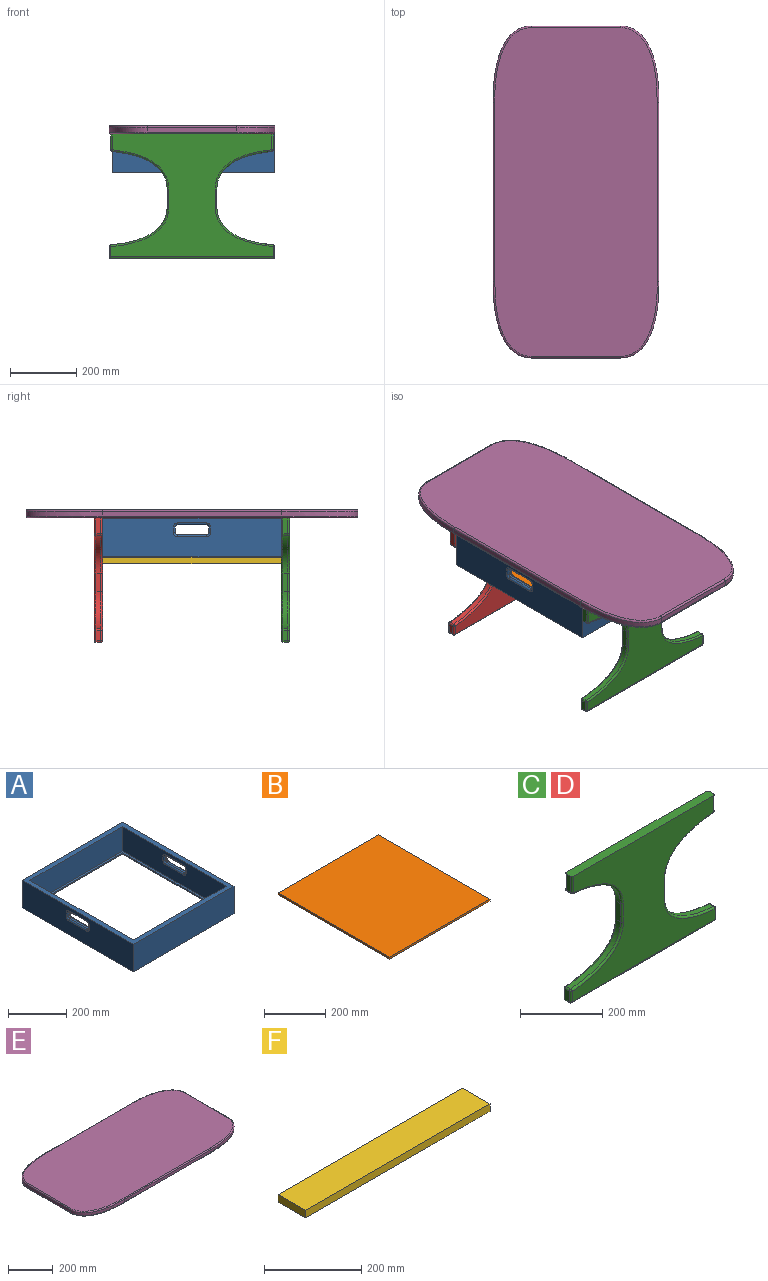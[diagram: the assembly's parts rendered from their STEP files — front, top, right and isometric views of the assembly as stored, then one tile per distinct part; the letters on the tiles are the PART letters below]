
ASSEMBLY  parts=6 mates=5
PART A: 68 faces, bbox 488x538x115 mm
  f0: plane 500x101.8mm, normal (1,0,0), area 46319.6mm2, adj f2,f3,f12,f27,f32,f33,f36,f37
  f1: plane 500x101.8mm, normal (-1,0,0), area 46319.6mm2, adj f2,f3,f12,f50,f51,f54,f55,f58
  f2: plane 450x101.8mm, normal (0,-1,0), area 45810mm2, adj f0,f1,f12,f62
  f3: plane 450x101.8mm, normal (0,1,0), area 45810mm2, adj f0,f1,f12,f62
  f4: plane 538x115mm, normal (-1,0,0), area 57289.6mm2, adj f8,f9,f12,f13,f22,f23,f24,f25
  f5: plane 500x5mm, normal (1,0,0), area 2500mm2, adj f10,f11,f13,f63
  f6: plane 500x5mm, normal (-1,0,0), area 2500mm2, adj f10,f11,f13,f63
  f7: plane 538x115mm, normal (1,0,0), area 57289.6mm2, adj f8,f9,f12,f13,f42,f43,f44,f46
  f8: plane 488x115mm, normal (0,1,0), area 56120mm2, adj f4,f7,f12,f13
  f9: plane 488x115mm, normal (0,-1,0), area 56120mm2, adj f4,f7,f12,f13
  f10: plane 450x5mm, normal (0,-1,0), area 2250mm2, adj f5,f6,f13,f63
  f11: plane 450x5mm, normal (0,1,0), area 2250mm2, adj f5,f6,f13,f63
  f12: plane 538x488mm, normal (0,0,1), area 37544mm2, adj f0,f1,f2,f3,f4,f7,f8,f9
  f13: plane 538x488mm, normal (0,0,-1), area 37544mm2, adj f4,f5,f6,f7,f8,f9,f10,f11
  f14: plane 18x7mm, normal (0,1,0), area 126mm2, adj f45,f46,f55,f56
  f15: plane 88x7mm, normal (0,0,1), area 616mm2, adj f42,f45,f49,f50
  f16: plane 18x7mm, normal (0,-1,0), area 126mm2, adj f48,f49,f57,f58
  f17: plane 88x7mm, normal (0,0,-1), area 616mm2, adj f47,f56,f57,f61
  f18: plane 88x7mm, normal (0,0,-1), area 616mm2, adj f30,f35,f38,f41
  f19: plane 18x7mm, normal (0,-1,0), area 126mm2, adj f28,f29,f37,f38
  f20: plane 88x7mm, normal (0,0,1), area 616mm2, adj f22,f26,f27,f28
  f21: plane 18x7mm, normal (0,1,0), area 126mm2, adj f25,f26,f35,f36
  f22: cylinder r=6mm len=88mm, axis (0,-1,0), area 829.4mm2, adj f4,f20,f23,f24
  f23: torus R=12mm, axis (1,0,0), area 121.1mm2, adj f4,f22,f25,f26
  f24: torus R=12mm, axis (1,0,0), area 121.1mm2, adj f4,f22,f28,f29
  f25: cylinder r=6mm len=18mm, axis (0,0,1), area 169.6mm2, adj f4,f21,f23,f31
  f26: cylinder r=6mm len=7mm, axis (-1,0,0), area 66mm2, adj f20,f21,f23,f32
  f27: cylinder r=6mm len=88mm, axis (0,-1,0), area 829.4mm2, adj f0,f20,f32,f33
  f28: cylinder r=6mm len=7mm, axis (1,0,0), area 66mm2, adj f19,f20,f24,f33
  f29: cylinder r=6mm len=18mm, axis (0,0,-1), area 169.6mm2, adj f4,f19,f24,f34
  f30: cylinder r=6mm len=88mm, axis (0,1,0), area 829.4mm2, adj f4,f18,f31,f34
  f31: torus R=12mm, axis (1,0,0), area 121.1mm2, adj f4,f25,f30,f35
  f32: torus R=12mm, axis (1,0,0), area 121.1mm2, adj f0,f26,f27,f36
  f33: torus R=12mm, axis (1,0,0), area 121.1mm2, adj f0,f27,f28,f37
  f34: torus R=12mm, axis (1,0,0), area 121.1mm2, adj f4,f29,f30,f38
  f35: cylinder r=6mm len=7mm, axis (1,0,0), area 66mm2, adj f18,f21,f31,f39
  f36: cylinder r=6mm len=18mm, axis (0,0,1), area 169.6mm2, adj f0,f21,f32,f39
  f37: cylinder r=6mm len=18mm, axis (0,0,-1), area 169.6mm2, adj f0,f19,f33,f40
  f38: cylinder r=6mm len=7mm, axis (-1,0,0), area 66mm2, adj f18,f19,f34,f40
  f39: torus R=12mm, axis (1,0,0), area 121.1mm2, adj f0,f35,f36,f41
  f40: torus R=12mm, axis (1,0,0), area 121.1mm2, adj f0,f37,f38,f41
  f41: cylinder r=6mm len=88mm, axis (0,1,0), area 829.4mm2, adj f0,f18,f39,f40
  f42: cylinder r=6mm len=88mm, axis (0,-1,0), area 829.4mm2, adj f7,f15,f43,f44
  f43: torus R=12mm, axis (1,0,0), area 121.1mm2, adj f7,f42,f45,f46
  f44: torus R=12mm, axis (1,0,0), area 121.1mm2, adj f7,f42,f48,f49
  f45: cylinder r=6mm len=7mm, axis (-1,0,0), area 66mm2, adj f14,f15,f43,f51
  f46: cylinder r=6mm len=18mm, axis (0,0,1), area 169.6mm2, adj f7,f14,f43,f52
  f47: cylinder r=6mm len=88mm, axis (0,1,0), area 829.4mm2, adj f7,f17,f52,f53
  f48: cylinder r=6mm len=18mm, axis (0,0,-1), area 169.6mm2, adj f7,f16,f44,f53
  f49: cylinder r=6mm len=7mm, axis (1,0,0), area 66mm2, adj f15,f16,f44,f54
  f50: cylinder r=6mm len=88mm, axis (0,1,0), area 829.4mm2, adj f1,f15,f51,f54
  f51: torus R=12mm, axis (1,0,0), area 121.1mm2, adj f1,f45,f50,f55
  f52: torus R=12mm, axis (1,0,0), area 121.1mm2, adj f7,f46,f47,f56
  f53: torus R=12mm, axis (1,0,0), area 121.1mm2, adj f7,f47,f48,f57
  f54: torus R=12mm, axis (1,0,0), area 121.1mm2, adj f1,f49,f50,f58
  f55: cylinder r=6mm len=18mm, axis (0,0,-1), area 169.6mm2, adj f1,f14,f51,f59
  f56: cylinder r=6mm len=7mm, axis (1,0,0), area 66mm2, adj f14,f17,f52,f59
  f57: cylinder r=6mm len=7mm, axis (-1,0,0), area 66mm2, adj f16,f17,f53,f60
  f58: cylinder r=6mm len=18mm, axis (0,0,1), area 169.6mm2, adj f1,f16,f54,f60
  f59: torus R=12mm, axis (1,0,0), area 121.1mm2, adj f1,f55,f56,f61
  f60: torus R=12mm, axis (1,0,0), area 121.1mm2, adj f1,f57,f58,f61
  f61: cylinder r=6mm len=88mm, axis (0,-1,0), area 829.4mm2, adj f1,f17,f59,f60
  f62: plane 516x466mm, normal (0,0,-1), area 15456mm2, adj f0,f1,f2,f3,f64,f65,f66,f67
  f63: plane 516x466mm, normal (0,0,1), area 15456mm2, adj f5,f6,f10,f11,f64,f65,f66,f67
  f64: plane 466x8.2mm, normal (0,1,0), area 3821.2mm2, adj f62,f63,f65,f67
  f65: plane 516x8.2mm, normal (1,0,0), area 4231.2mm2, adj f62,f63,f64,f66
  f66: plane 466x8.2mm, normal (0,-1,0), area 3821.2mm2, adj f62,f63,f65,f67
  f67: plane 516x8.2mm, normal (-1,0,0), area 4231.2mm2, adj f62,f63,f64,f66
PART B: 6 faces, bbox 464.5x513.9x7.9 mm
  f0: plane 464.5x7.9mm, normal (0,-1,0), area 3669.6mm2, adj f1,f3,f4,f5
  f1: plane 513.89x7.9mm, normal (-1,0,0), area 4059.8mm2, adj f0,f2,f4,f5
  f2: plane 464.5x7.9mm, normal (0,1,0), area 3669.6mm2, adj f1,f3,f4,f5
  f3: plane 513.89x7.9mm, normal (1,0,0), area 4059.8mm2, adj f0,f2,f4,f5
  f4: plane 513.89x464.5mm, normal (0,0,-1), area 238703.2mm2, adj f0,f1,f2,f3
  f5: plane 513.89x464.5mm, normal (0,0,1), area 238703.2mm2, adj f0,f1,f2,f3
PART C: 54 faces, bbox 500x25x375 mm
  f0: plane 47.9x15mm, normal (-1,0,0), area 718.5mm2, adj f11,f47,f50,f53
  f1: extruded ~165.48x113.16mm, area 3308.5mm2, adj f2,f48,f49,f53
  f2: plane 55x15mm, normal (-1,0,0), area 825mm2, adj f1,f3,f45,f46
  f3: extruded ~170.42x113.6mm, area 3383mm2, adj f2,f39,f43,f44
  f4: plane 30.38x15mm, normal (-1,0,0), area 455.7mm2, adj f34,f38,f39,f40
  f5: plane 490x15mm, normal (0,0,-1), area 7350mm2, adj f29,f33,f34,f35
  f6: plane 30.38x15mm, normal (1,0,0), area 455.7mm2, adj f24,f28,f29,f30
  f7: extruded ~170.42x113.6mm, area 3383mm2, adj f8,f23,f24,f25
  f8: plane 55x15mm, normal (1,0,0), area 825mm2, adj f7,f9,f21,f22
  f9: extruded ~165.48x113.16mm, area 3308.5mm2, adj f8,f15,f19,f20
  f10: plane 47.9x15mm, normal (1,0,0), area 718.5mm2, adj f11,f14,f15,f16
  f11: plane 490x25mm, normal (0,0,1), area 12228.5mm2, adj f0,f10,f12,f13,f14,f16,f47,f50
  f12: plane 490.04x370mm, normal (0,-1,0), area 96719.7mm2, adj f11,f14,f19,f21,f23,f28,f33,f38
  f13: plane 490.04x370mm, normal (0,1,0), area 96719.7mm2, adj f11,f16,f20,f22,f25,f30,f35,f40
  f14: cylinder r=5mm len=47.9mm, axis (0,0,-1), area 376.2mm2, adj f10,f11,f12,f17
  f15: cylinder r=5mm len=15mm, axis (0,1,0), area 110.6mm2, adj f9,f10,f17,f18
  f16: cylinder r=5mm len=47.9mm, axis (0,0,1), area 376.2mm2, adj f10,f11,f13,f18
  f17: sphere r=5mm, area 36.9mm2, adj f14,f15,f19
  f18: sphere r=5mm, area 36.9mm2, adj f15,f16,f20
  f19: bspline ~179x174.15mm, area 1753.5mm2, adj f9,f12,f17,f21
  f20: bspline ~179x174.15mm, area 1753.5mm2, adj f9,f13,f18,f22
  f21: cylinder r=5mm len=55mm, axis (0,0,-1), area 432mm2, adj f8,f12,f19,f23
  f22: cylinder r=5mm len=55mm, axis (0,0,1), area 432mm2, adj f8,f13,f20,f25
  f23: bspline ~182.13x176.56mm, area 1792.5mm2, adj f7,f12,f21,f26
  f24: cylinder r=5mm len=15mm, axis (0,1,0), area 111.5mm2, adj f6,f7,f26,f27
  f25: bspline ~182.13x176.56mm, area 1792.5mm2, adj f7,f13,f22,f27
  f26: sphere r=5mm, area 37.2mm2, adj f23,f24,f28
  f27: sphere r=5mm, area 37.2mm2, adj f24,f25,f30
  f28: cylinder r=5mm len=30.38mm, axis (0,0,-1), area 238.6mm2, adj f6,f12,f26,f31
  f29: cylinder r=5mm len=15mm, axis (0,-1,0), area 117.8mm2, adj f5,f6,f31,f32
  f30: cylinder r=5mm len=30.38mm, axis (0,0,1), area 238.6mm2, adj f6,f13,f27,f32
  f31: sphere r=5mm, area 39.3mm2, adj f28,f29,f33
  f32: sphere r=5mm, area 39.3mm2, adj f29,f30,f35
  f33: cylinder r=5mm len=490mm, axis (-1,0,0), area 3848.5mm2, adj f5,f12,f31,f36
  f34: cylinder r=5mm len=15mm, axis (0,1,0), area 117.8mm2, adj f4,f5,f36,f37
  f35: cylinder r=5mm len=490mm, axis (1,0,0), area 3848.5mm2, adj f5,f13,f32,f37
  f36: sphere r=5mm, area 39.3mm2, adj f33,f34,f38
  f37: sphere r=5mm, area 39.3mm2, adj f34,f35,f40
  f38: cylinder r=5mm len=30.38mm, axis (0,0,1), area 238.6mm2, adj f4,f12,f36,f41
  f39: cylinder r=5mm len=15mm, axis (0,1,0), area 111.5mm2, adj f3,f4,f41,f42
  f40: cylinder r=5mm len=30.38mm, axis (0,0,-1), area 238.6mm2, adj f4,f13,f37,f42
  f41: sphere r=5mm, area 37.2mm2, adj f38,f39,f43
  f42: sphere r=5mm, area 37.2mm2, adj f39,f40,f44
  f43: bspline ~182.13x176.56mm, area 1792.5mm2, adj f3,f12,f41,f45
  f44: bspline ~182.13x176.56mm, area 1792.5mm2, adj f3,f13,f42,f46
  f45: cylinder r=5mm len=55mm, axis (0,0,1), area 432mm2, adj f2,f12,f43,f48
  f46: cylinder r=5mm len=55mm, axis (0,0,-1), area 432mm2, adj f2,f13,f44,f49
  f47: cylinder r=5mm len=47.9mm, axis (0,0,1), area 376.2mm2, adj f0,f11,f12,f51
  f48: bspline ~179x174.15mm, area 1753.5mm2, adj f1,f12,f45,f51
  f49: bspline ~179x174.15mm, area 1753.5mm2, adj f1,f13,f46,f52
  f50: cylinder r=5mm len=47.9mm, axis (0,0,-1), area 376.2mm2, adj f0,f11,f13,f52
  f51: sphere r=5mm, area 36.9mm2, adj f47,f48,f53
  f52: sphere r=5mm, area 36.9mm2, adj f49,f50,f53
  f53: cylinder r=5mm len=15mm, axis (0,1,0), area 110.6mm2, adj f0,f1,f51,f52
PART D: same geometry as C
PART E: 26 faces, bbox 1000x500x25 mm
  f0: extruded ~230x115mm, area 4255.4mm2, adj f1,f7,f14,f22
  f1: plane 540x15mm, normal (0,-1,0), area 8100mm2, adj f0,f2,f12,f20
  f2: extruded ~230x115mm, area 4255.4mm2, adj f1,f3,f10,f18
  f3: plane 270x15mm, normal (1,0,0), area 4050mm2, adj f2,f4,f11,f19
  f4: extruded ~230x115mm, area 4255.4mm2, adj f3,f5,f13,f21
  f5: plane 540x15mm, normal (0,1,0), area 8100mm2, adj f4,f6,f15,f23
  f6: extruded ~230x115mm, area 4255.4mm2, adj f5,f7,f17,f25
  f7: plane 270x15mm, normal (-1,0,0), area 4050mm2, adj f0,f6,f16,f24
  f8: plane 990x490mm, normal (0,0,1), area 467205.9mm2, adj f18,f19,f20,f21,f22,f23,f24,f25
  f9: plane 990x490mm, normal (0,0,-1), area 467205.9mm2, adj f10,f11,f12,f13,f14,f15,f16,f17
  f10: bspline ~375.92x127.41mm, area 2205.7mm2, adj f2,f9,f11,f12
  f11: cylinder r=5mm len=270mm, axis (0,1,0), area 2120.6mm2, adj f3,f9,f10,f13
  f12: cylinder r=5mm len=540mm, axis (1,0,0), area 4241.2mm2, adj f1,f9,f10,f14
  f13: bspline ~375.92x122.76mm, area 2205.6mm2, adj f4,f9,f11,f15
  f14: bspline ~375.92x122.76mm, area 2205.6mm2, adj f0,f9,f12,f16
  f15: cylinder r=5mm len=540mm, axis (-1,0,0), area 4241.2mm2, adj f5,f9,f13,f17
  f16: cylinder r=5mm len=270mm, axis (0,-1,0), area 2120.6mm2, adj f7,f9,f14,f17
  f17: bspline ~375.92x127.41mm, area 2205.7mm2, adj f6,f9,f15,f16
  f18: bspline ~375.92x122.76mm, area 2205.6mm2, adj f2,f8,f19,f20
  f19: cylinder r=5mm len=270mm, axis (0,-1,0), area 2120.6mm2, adj f3,f8,f18,f21
  f20: cylinder r=5mm len=540mm, axis (-1,0,0), area 4241.2mm2, adj f1,f8,f18,f22
  f21: bspline ~375.92x127.41mm, area 2205.7mm2, adj f4,f8,f19,f23
  f22: bspline ~375.92x127.41mm, area 2205.7mm2, adj f0,f8,f20,f24
  f23: cylinder r=5mm len=540mm, axis (1,0,0), area 4241.2mm2, adj f5,f8,f21,f25
  f24: cylinder r=5mm len=270mm, axis (0,1,0), area 2120.6mm2, adj f7,f8,f22,f25
  f25: bspline ~375.92x122.76mm, area 2205.6mm2, adj f6,f8,f23,f24
PART F: 6 faces, bbox 538x80x19 mm
  f0: plane 538x19mm, normal (0,1,0), area 10222mm2, adj f1,f3,f4,f5
  f1: plane 80x19mm, normal (-1,0,0), area 1520mm2, adj f0,f2,f4,f5
  f2: plane 538x19mm, normal (0,-1,0), area 10222mm2, adj f1,f3,f4,f5
  f3: plane 80x19mm, normal (1,0,0), area 1520mm2, adj f0,f2,f4,f5
  f4: plane 538x80mm, normal (0,0,1), area 43040mm2, adj f0,f1,f2,f3
  f5: plane 538x80mm, normal (0,0,-1), area 43040mm2, adj f0,f1,f2,f3
PLACE A t=(-78.93,-337.53,1.99)mm
PLACE B t=(-79.43,-337.48,2.29)mm
PLACE C rot(axis=(1,0,0),0deg) t=(-82.34,-606.6,-96.7)mm
PLACE D t=(-82.34,-43.1,-96.7)mm
PLACE E rot(axis=(0,0,-1),90deg) t=(-82.34,-337.6,118.3)mm
PLACE F rot(axis=(0,0,1),90deg) t=(-47.34,-368.56,-19.57)mm
MATE planar B.f5 <-> A.f62  axis (0,0,1) through (-79.68,-337.53,15.19)mm
MATE planar B.f1 <-> A.f65  axis (-1,0,0) through (-311.93,-337.53,11.24)mm
MATE planar C.f11 <-> E.f9  axis (0,0,1) through (-82.34,-619.1,118.3)mm
MATE planar F.f1 <-> C.f13  axis (0,-1,0) through (-87.34,-606.6,-10.07)mm
MATE planar E.f9 <-> D.f11  axis (0,0,-1) through (-82.34,-337.6,118.3)mm
